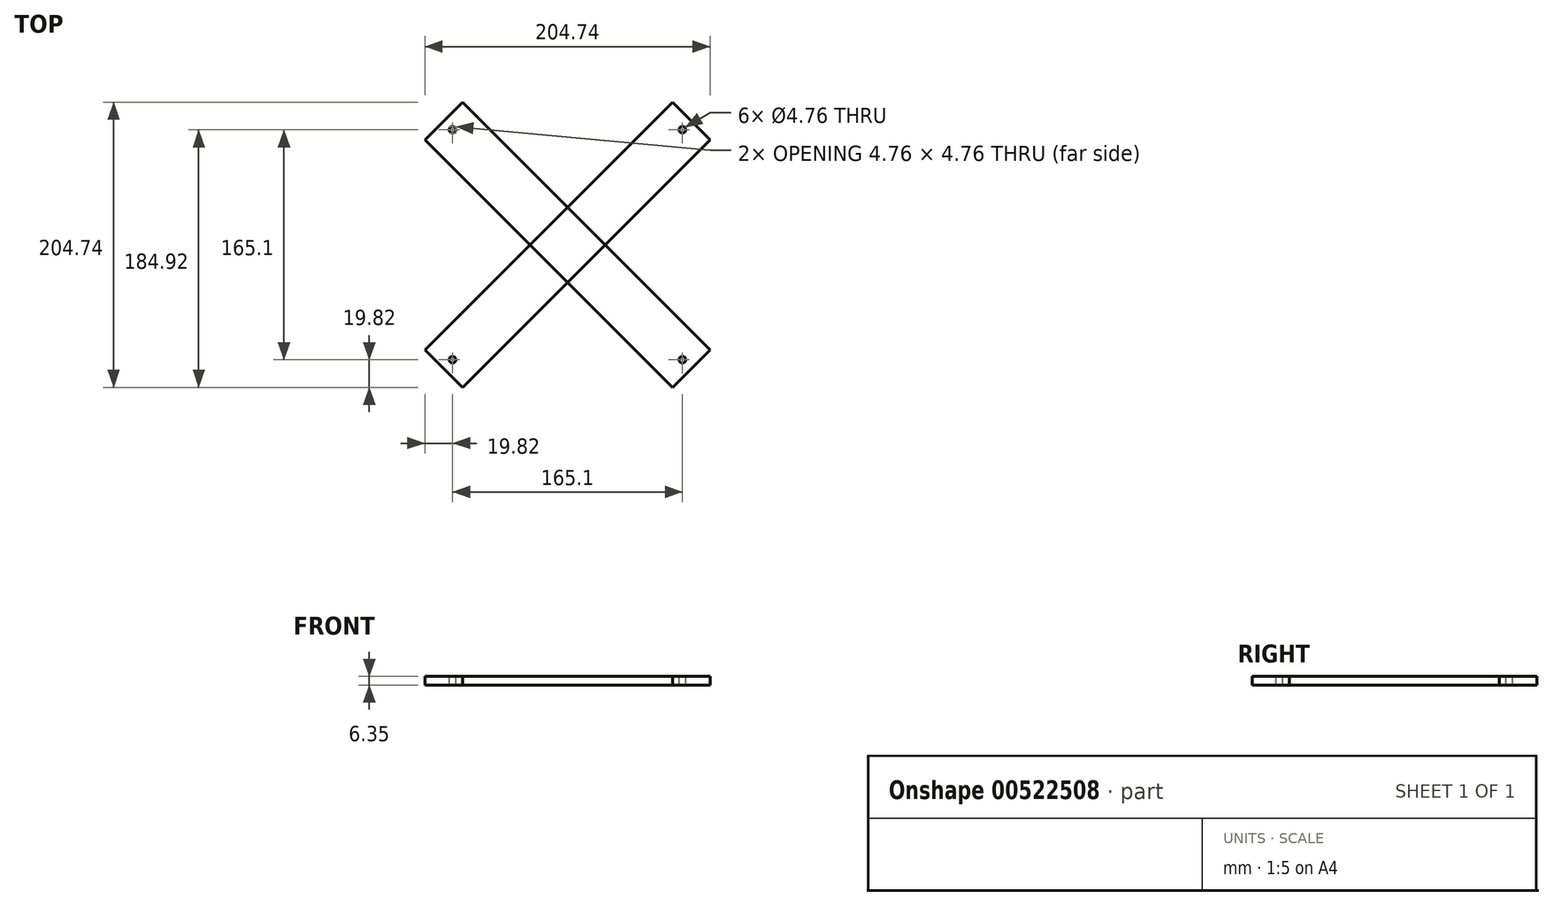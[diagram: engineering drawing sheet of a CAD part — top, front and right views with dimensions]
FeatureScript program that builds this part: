
annotation { "Feature Type Name" : "Feature", "Feature Type Description" : "" }
export const myFeature = defineFeature(function(context is Context, id is Id, definition is map)
    precondition{}
    {
        {
            var Q0;
            Q0=qCreatedBy(makeId("Top.planeOp"),FACE);
            var sketch = newSketch(context, id + "F0", { "sketchPlane" : qUnion([Q0])});
            skLineSegment(sketch, "E0.bottom", {"start": v(88.9, 88.9) * mm, "end": v(-88.9, 88.9) * mm, "construction": true});
            skLineSegment(sketch, "E0.top", {"start": v(88.9, -88.9) * mm, "end": v(-88.9, -88.9) * mm, "construction": true});
            skLineSegment(sketch, "E0.left", {"start": v(88.9, 88.9) * mm, "end": v(88.9, -88.9) * mm, "construction": true});
            skLineSegment(sketch, "E0.right", {"start": v(-88.9, 88.9) * mm, "end": v(-88.9, -88.9) * mm, "construction": true});
            skPoint(sketch, "E0.middle", {"position": v(0, 0) * mm});
            skLineSegment(sketch, "E1", {"start": v(-88.9, -88.9) * mm, "end": v(88.9, 88.9) * mm});
            skLineSegment(sketch, "E2.bottom", {"start": v(82.55, 82.55) * mm, "end": v(-82.55, 82.55) * mm, "construction": true});
            skLineSegment(sketch, "E2.top", {"start": v(82.55, -82.55) * mm, "end": v(-82.55, -82.55) * mm, "construction": true});
            skLineSegment(sketch, "E2.left", {"start": v(82.55, 82.55) * mm, "end": v(82.55, -82.55) * mm, "construction": true});
            skLineSegment(sketch, "E2.right", {"start": v(-82.55, 82.55) * mm, "end": v(-82.55, -82.55) * mm, "construction": true});
            skLineSegment(sketch, "E3", {"start": v(-82.55, 82.55) * mm, "end": v(82.55, -82.55) * mm, "construction": true});
            skSolve(sketch);
        }
        {
            var Q0;
            Q0=sQuery(id+"F0.wireOp",EDGE,"E1");
            extrude(context, id + "F1", {"bodyType" : ToolBodyType.SURFACE, "surfaceEntities" : qUnion([Q0]), "oppositeDirection" : true, "depth" : 6.35 * mm, "offsetDistance" : 25.4 * mm});
        }
        {
            var Q0;
            Q0=makeQuery(id+"F1.opExtrude","SWEPT_FACE",FACE,{"disambiguationData":[OSD([sQuery(id+"F0.wireOp",EDGE,"E1")])]});
            extrude(context, id + "F2", {"entities" : qUnion([Q0]), "depth" : 19.05 * mm, "offsetDistance" : 25.4 * mm, "hasSecondDirection" : true, "secondDirectionOppositeDirection" : true, "secondDirectionDepth" : 19.05 * mm});
        }
        {
            var Q0;
            Q0=sQuery(id+"F0.wireOp",VERTEX,"E2.top.end");
            var Q1;
            Q1=sQuery(id+"F0.wireOp",VERTEX,"E2.left.start");
            var Q2;
            Q2=makeQuery(id+"F2.opExtrude","SWEPT_BODY",BODY,{"disambiguationData":[OSD([sQuery(id+"F0.wireOp",EDGE,"E1")])]});
            hole(context, id + "F3", {"style" : HoleStyle.SIMPLE, "endStyle" : HoleEndStyle.THROUGH, "holeDiameter" : 4.76 * mm, "isTappedThrough" : true, "tappedDepth" : 12.7 * mm, "tapClearance" : 3, "locations" : qUnion([Q0, Q1]), "scope" : qUnion([Q2])});
        }
        {
            var Q0;
            Q0=qCreatedBy(makeId("Front.planeOp"),FACE);
            var sketch = newSketch(context, id + "F4", { "sketchPlane" : qUnion([Q0])});
            skLineSegment(sketch, "E4", {"start": v(0, 0) * mm, "end": v(0, 47.13) * mm});
            skSolve(sketch);
        }
        {
            var Q0;
            Q0=makeQuery(id+"F2.opExtrude","SWEPT_BODY",BODY,{"disambiguationData":[OSD([sQuery(id+"F0.wireOp",EDGE,"E1")])]});
            var Q1;
            Q1=sQuery(id+"F4.wireOp",EDGE,"E4");
            circularPattern(context, id + "F5", {"entities" : qUnion([Q0]), "axis" : qUnion([Q1]), "angle" : 90 * degree, "instanceCount" : 2, "equalSpace" : true, "isCentered" : true});
        }
    });
